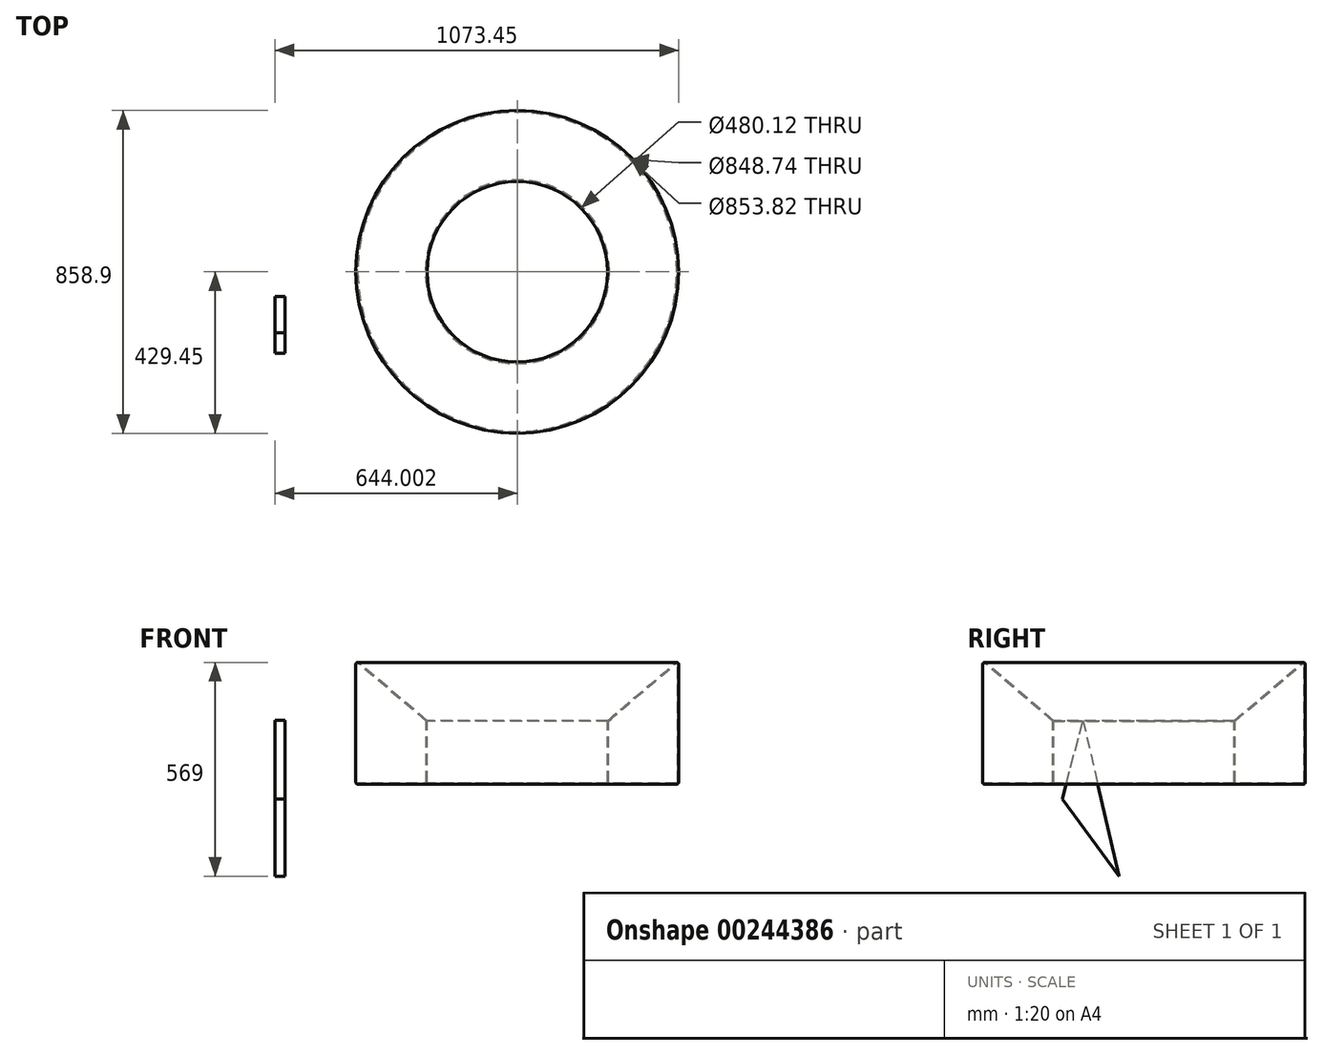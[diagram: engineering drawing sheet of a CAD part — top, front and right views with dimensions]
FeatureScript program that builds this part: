
annotation { "Feature Type Name" : "Feature", "Feature Type Description" : "" }
export const myFeature = defineFeature(function(context is Context, id is Id, definition is map)
    precondition{}
    {
        {
            var Q0;
            Q0=qCreatedBy(makeId("Front.planeOp"),FACE);
            var sketch = newSketch(context, id + "F0", { "sketchPlane" : qUnion([Q0])});
            skLineSegment(sketch, "E0.bottom", {"start": v(-94.14, 59.96) * mm, "end": v(71.24, 59.96) * mm});
            skLineSegment(sketch, "E0.top", {"start": v(-94.14, -64.45) * mm, "end": v(71.24, -64.45) * mm});
            skLineSegment(sketch, "E0.left", {"start": v(-94.14, 59.96) * mm, "end": v(-94.14, -64.45) * mm});
            skLineSegment(sketch, "E0.right", {"start": v(71.24, 59.96) * mm, "end": v(71.24, -64.45) * mm});
            skSolve(sketch);
        }
        {
            var Q0;
            Q0=qSketchRegion(id+"F0",true);
            extrude(context, id + "F1", {"entities" : qUnion([Q0]), "depth" : 25.4 * mm});
        }
        {
            var Q0;
            Q0=qCreatedBy(makeId("Right.planeOp"),FACE);
            var sketch = newSketch(context, id + "F2", { "sketchPlane" : qUnion([Q0])});
            skLineSegment(sketch, "E1", {"start": v(-217.06, 0) * mm, "end": v(-162.24, 209.26) * mm});
            skLineSegment(sketch, "E2", {"start": v(-162.24, 209.26) * mm, "end": v(-65.82, -205.6) * mm});
            skLineSegment(sketch, "E3", {"start": v(-65.82, -205.6) * mm, "end": v(-217.06, 0) * mm});
            skSolve(sketch);
        }
        {
            var Q0;
            Q0=qCreatedBy(makeId("Right.planeOp"),FACE);
            var sketch = newSketch(context, id + "F3", { "sketchPlane" : qUnion([Q0])});
            skLineSegment(sketch, "E4.bottom", {"start": v(70.64, 281.63) * mm, "end": v(186.26, 281.63) * mm});
            skLineSegment(sketch, "E4.top", {"start": v(70.64, 155.46) * mm, "end": v(186.26, 155.46) * mm});
            skLineSegment(sketch, "E4.left", {"start": v(70.64, 281.63) * mm, "end": v(70.64, 155.46) * mm});
            skLineSegment(sketch, "E4.right", {"start": v(186.26, 281.63) * mm, "end": v(186.26, 155.46) * mm});
            skLineSegment(sketch, "E5.bottom", {"start": v(15.1, 155.2) * mm, "end": v(185.64, 155.2) * mm});
            skLineSegment(sketch, "E5.top", {"start": v(15.1, -64.15) * mm, "end": v(185.64, -64.15) * mm});
            skLineSegment(sketch, "E5.left", {"start": v(15.1, 155.2) * mm, "end": v(15.1, -64.15) * mm});
            skLineSegment(sketch, "E5.right", {"start": v(185.64, 155.2) * mm, "end": v(185.64, -64.15) * mm});
            skSolve(sketch);
        }
        {
            var Q0;
            Q0=qSketchRegion(id+"F3",true);
            var Q1;
            Q1=makeQuery(id+"F1.opExtrude","CAP_EDGE",EDGE,{"disambiguationData":[OSD([sQuery(id+"F0.wireOp",EDGE,"E0.right")])],"isStart":false});
            revolve(context, id + "F11", {"operationType" : NewBodyOperationType.ADD, "entities" : qUnion([Q0]), "axis" : qUnion([Q1]), "revolveType" : RevolveType.FULL});
        }
        {
            var Q0;
            Q0=makeQuery(id+"F11.opRevolve","SWEPT_FACE",FACE,{"disambiguationData":[OSD([sQuery(id+"F3.wireOp",EDGE,"E4.bottom")])]});
            var Q1;
            Q1=makeQuery(id+"F11.opRevolve","SWEPT_FACE",FACE,{"disambiguationData":[OSD([sQuery(id+"F3.wireOp",EDGE,"E5.bottom")])]});
            shell(context, id + "F4", {"entities" : qUnion([Q0, Q1]), "thickness" : 2.54 * mm});
        }
        {
            var Q0;
            Q0=makeQuery(id+"F11.opRevolve","SWEPT_BODY",BODY,{"disambiguationData":[OSD([sQuery(id+"F3.wireOp",EDGE,"E4.bottom"),sQuery(id+"F3.wireOp",EDGE,"E4.top"),sQuery(id+"F3.wireOp",EDGE,"E4.left"),sQuery(id+"F3.wireOp",EDGE,"E4.right")])]});
            var Q1;
            Q1=makeQuery(id+"F1.opExtrude","SWEPT_BODY",BODY,{"disambiguationData":[OSD([sQuery(id+"F0.wireOp",EDGE,"E0.bottom"),sQuery(id+"F0.wireOp",EDGE,"E0.top"),sQuery(id+"F0.wireOp",EDGE,"E0.left"),sQuery(id+"F0.wireOp",EDGE,"E0.right")])]});
            deleteBodies(context, id + "F5", {"entities" : qUnion([Q0, Q1])});
        }
        {
            var Q0;
            Q0=qSketchRegion(id+"F2",true);
            extrude(context, id + "F6", {"entities" : qUnion([Q0]), "depth" : 25.4 * mm});
        }
        {
            var Q0;
            Q0=qCreatedBy(makeId("Front.planeOp"),FACE);
            var sketch = newSketch(context, id + "F7", { "sketchPlane" : qUnion([Q0])});
            skLineSegment(sketch, "E6.bottom", {"start": v(403.94, 208.47) * mm, "end": v(214.55, 208.47) * mm});
            skLineSegment(sketch, "E6.top", {"start": v(403.94, 39.47) * mm, "end": v(214.55, 39.47) * mm});
            skLineSegment(sketch, "E6.left", {"start": v(403.94, 208.47) * mm, "end": v(403.94, 39.47) * mm});
            skLineSegment(sketch, "E6.right", {"start": v(214.55, 208.47) * mm, "end": v(214.55, 39.47) * mm});
            skLineSegment(sketch, "E7", {"start": v(403.94, 208.47) * mm, "end": v(214.55, 369.31) * mm});
            skLineSegment(sketch, "E8", {"start": v(214.55, 369.31) * mm, "end": v(214.55, 208.47) * mm});
            skLineSegment(sketch, "E9", {"start": v(644, 546.05) * mm, "end": v(644, -209.93) * mm, "construction": true});
            skSolve(sketch);
        }
        {
            var Q0;
            Q0=qSketchRegion(id+"F7",true);
            var Q1;
            Q1=sQuery(id+"F7.wireOp",EDGE,"E9");
            revolve(context, id + "F8", {"entities" : qUnion([Q0]), "axis" : qUnion([Q1]), "revolveType" : RevolveType.FULL});
        }
        {
            var Q0;
            Q0=makeQuery(id+"F8.opRevolve","SWEPT_EDGE",EDGE,{"disambiguationData":[OSD([sQuery(id+"F7.wireOp",EDGE,"E7"),sQuery(id+"F7.wireOp",EDGE,"E8")])]});
            var Q1;
            Q1=makeQuery(id+"F8.opRevolve","SWEPT_FACE",FACE,{"disambiguationData":[OSD([sQuery(id+"F7.wireOp",EDGE,"E6.top")])]});
            fillet(context, id + "F9", {"entities" : qUnion([Q0, Q1]), "radius" : 5.08 * mm, "tangentPropagation" : true, "allowEdgeOverflow" : false});
        }
        {
            var Q0;
            Q0=makeQuery(id+"F8.opRevolve","SWEPT_FACE",FACE,{"disambiguationData":[OSD([sQuery(id+"F7.wireOp",EDGE,"E6.top")])]});
            shell(context, id + "F10", {"entities" : qUnion([Q0]), "thickness" : 2.54 * mm});
        }
    });
